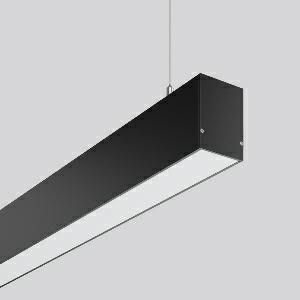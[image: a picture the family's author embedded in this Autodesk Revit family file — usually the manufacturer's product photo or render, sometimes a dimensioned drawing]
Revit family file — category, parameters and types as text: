
# Revit family: less_is_more_50_312313_003_76_7fce
name_source: partatom
category: Lighting Fixtures
units: mm (PartAtom-declared; Revit-internal decimal feet)

## family parameters
Cut with Voids When Loaded = No
Host = Face
Light Source = No
Part Type = Normal
Room Calculation Point = No
Round Connector Dimension = Use Diameter
Shared = No

## types (1)
- LESS IS MORE 50 (1 x LED Modul 830, 3850 lm, 3000)
    Apparent Load = 34 VA
    CIE Flux Codes = 48 79 95 100 100
    Color Rendering = 80
    Color Temperature = 3000
    Default Elevation = 1800 mm
    Description = Series: LESS IS MORE 50
Linear pendant luminaire for aesthetically sophisticated lighting. Housing: extruded aluminium profile, powder-coated. End cap aluminium powder-coated. Canopy made of aluminium, powder-coated. Diffuser made of non-yellowing plastic (PMMA), opal. Direct light emission. Suitable for pendant. 2-point steel cable suspension freely positionable and infinitely height-adjustable. Special lengths available on request. LED unit with integrated converter interchangeable and removable. Suitable for through-wiring. With sensors or as a safety luminaire on request. 
Colour: deep black, matt (RAL 9005)
Length: 1407 mm
Width: 57 mm
Height: 75 mm
Suspension length: 2000 mm
Lamp: LED
Socket: without socket
Colour temperature: 3000K
Colour rendering index (CRI): 80
System power: 34 W
Rated luminous flux: 3850 lm
Luminous efficiency: 113 lm/W
Control gear: Converter, dimmable, DALI
Protection class: I
Type of protection: IP 20
    Height = 75 mm
    Lamp = 1 x LED Modul 830
    Lamp Light Flux = 3850 lm
    Lamp count = 1
    Length = 1407 mm
    Lifetime = 50000 h
    Luminous efficacy = 113 lm/W
    Manufacturer = RZB
    ModVariant = No
    Model = 312313.003.76
    Mounting Place = Ceiling
    Mounting Type = Pendant
    Number of Poles = 1
    OnlyDefault = Yes
    Power Factor = 1
    Product Name = LESS IS MORE 50
    Product group = Pendant LED linear luminaires
    ProductGroupID = 907
    Protection Class = Protection class I
    Protection Degree = IP 20
    RLX_Detail_Level = 1
    RLX_Emergency_Light_Flux = 0 lm
    RLX_Emergency_Type = 0
    RLX_Emergency_Type_DB = No
    RlxData = <blob elided: 28897 chars, md5=eccb1ca9>
    Socket = socket
    Standby Power = 0 W
    System Light Flux = 3850 lm
    System Power = 34 W
    Type Comments = Product without accessories
    Type Image = 312318.003.jpg
    URL = http://relux.com
    VarID = ---
    Voltage = 230 V
    Voltage Range = 220-240 V
    Weight = 0.00 kg
    Width = 57 mm

## geometry (parser evidence)
native form markers: Blend x4, Sweep x8
no freeform markers — native parametric forms only
